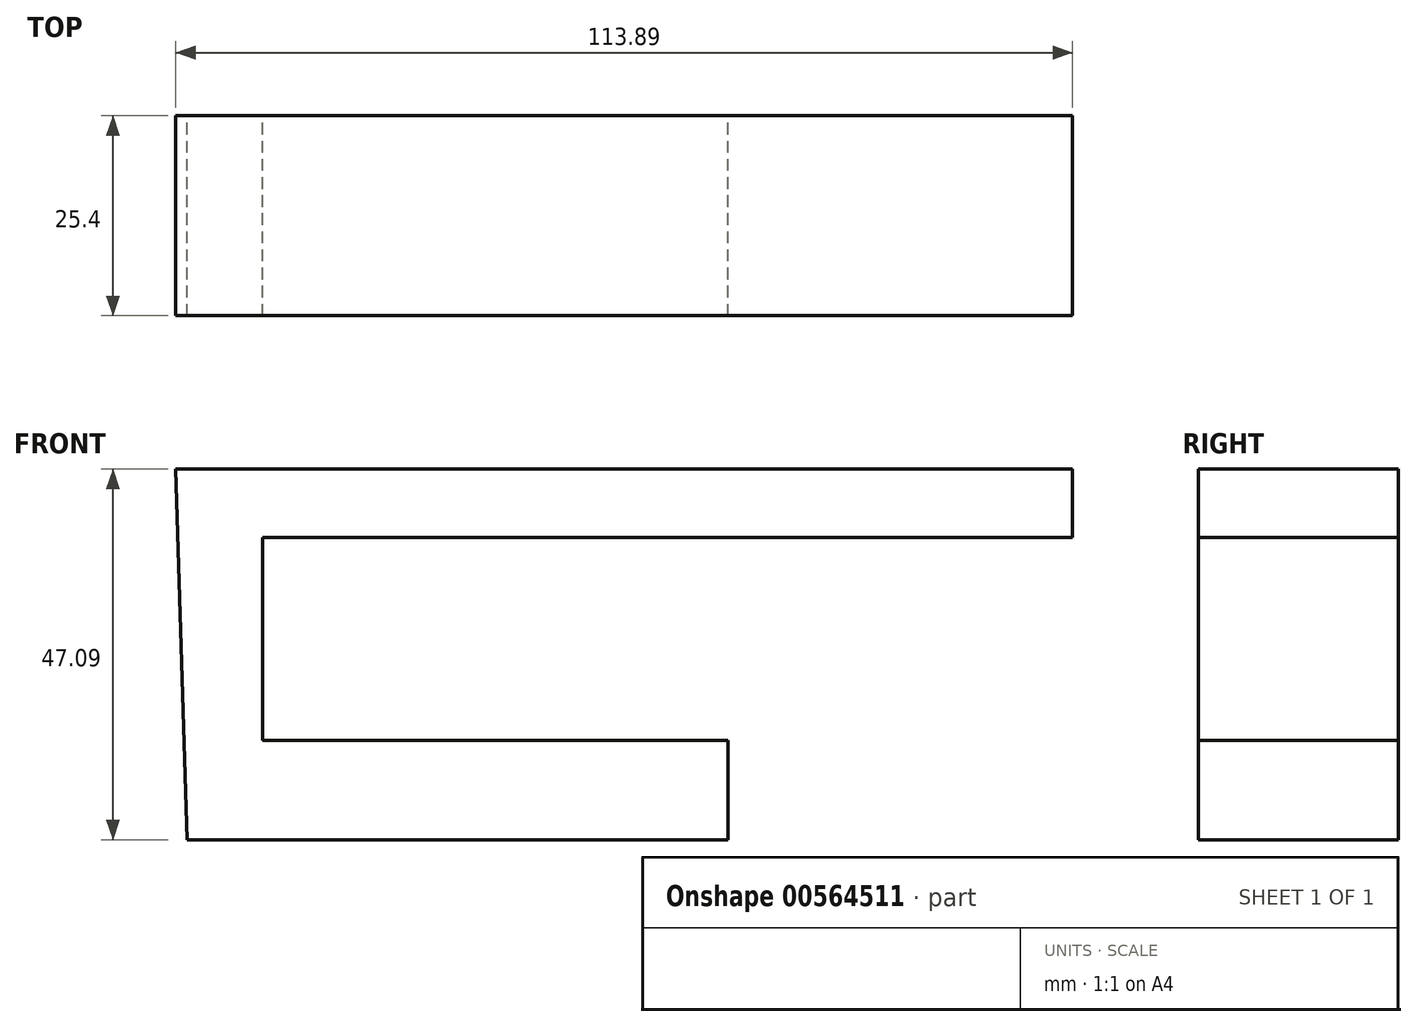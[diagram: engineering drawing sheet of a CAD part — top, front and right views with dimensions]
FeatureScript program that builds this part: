
annotation { "Feature Type Name" : "Feature", "Feature Type Description" : "" }
export const myFeature = defineFeature(function(context is Context, id is Id, definition is map)
    precondition{}
    {
        {
            var Q0;
            Q0=qCreatedBy(makeId("Front.planeOp"),FACE);
            var sketch = newSketch(context, id + "F0", { "sketchPlane" : qUnion([Q0])});
            skLineSegment(sketch, "E0", {"start": v(-54.56, 47.1) * mm, "end": v(59.33, 47.1) * mm});
            skLineSegment(sketch, "E1", {"start": v(59.33, 47.1) * mm, "end": v(59.33, 38.38) * mm});
            skLineSegment(sketch, "E2", {"start": v(59.33, 38.38) * mm, "end": v(-43.57, 38.38) * mm});
            skLineSegment(sketch, "E3", {"start": v(-43.57, 38.38) * mm, "end": v(-43.57, 12.65) * mm});
            skLineSegment(sketch, "E4", {"start": v(-43.57, 12.65) * mm, "end": v(15.56, 12.65) * mm});
            skLineSegment(sketch, "E5", {"start": v(15.56, 12.65) * mm, "end": v(15.56, 0) * mm});
            skLineSegment(sketch, "E6", {"start": v(15.56, 0) * mm, "end": v(-53.1, 0) * mm});
            skLineSegment(sketch, "E7", {"start": v(-53.1, 0) * mm, "end": v(-54.56, 47.1) * mm});
            skSolve(sketch);
        }
        {
            var Q0;
            Q0=makeQuery(id+"F0.imprint","IMPRINT",FACE,{"disambiguationData":[TD([[makeQuery(id+"F0.imprint","IMPRINT",EDGE,{"derivedFrom":sQuery(id+"F0.wireOp",EDGE,"E0")}),-1.0]])]});
            extrude(context, id + "F1", {"entities" : qUnion([Q0]), "depth" : 25.4 * mm, "offsetDistance" : 25.4 * mm});
        }
    });
